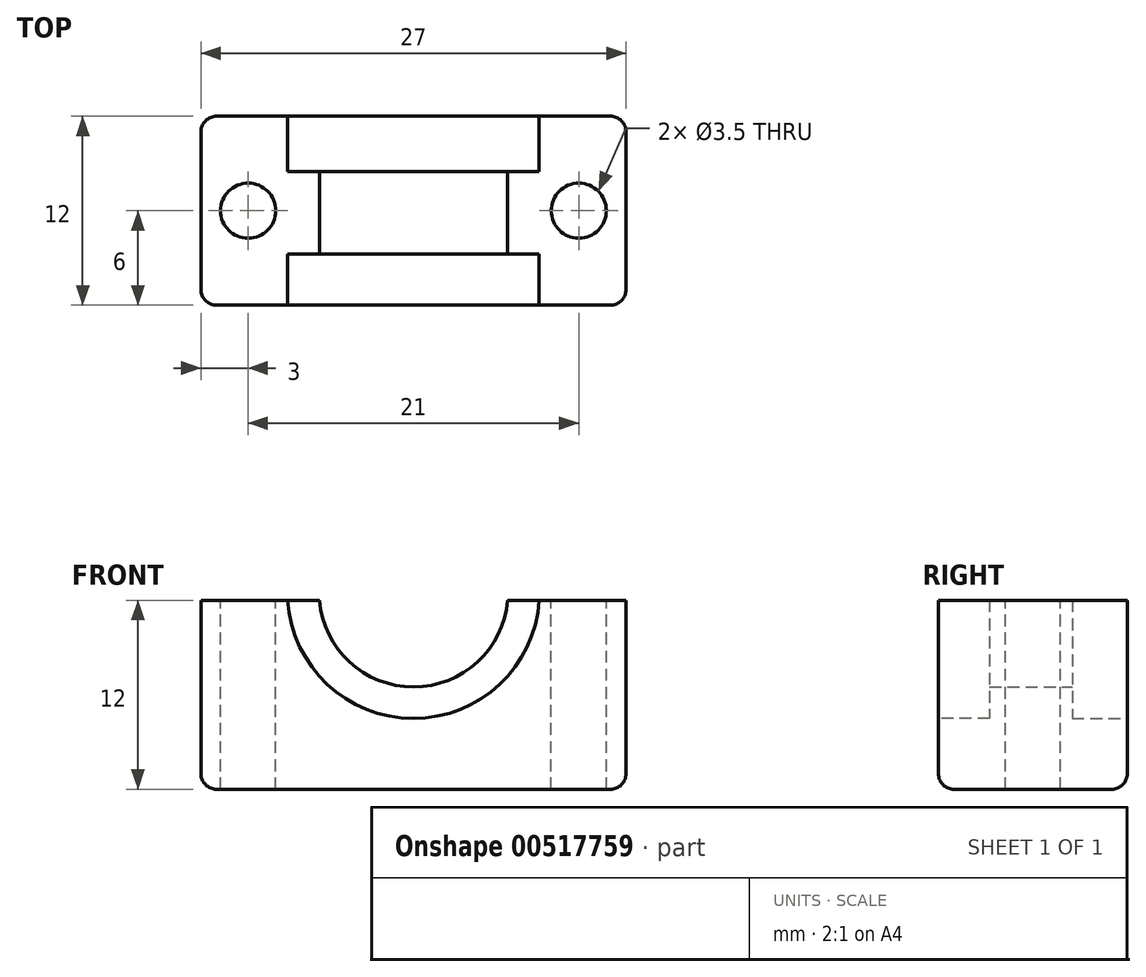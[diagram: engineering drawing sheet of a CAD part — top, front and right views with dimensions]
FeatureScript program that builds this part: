
annotation { "Feature Type Name" : "Feature", "Feature Type Description" : "" }
export const myFeature = defineFeature(function(context is Context, id is Id, definition is map)
    precondition{}
    {
        {
            var Q0;
            Q0=qCreatedBy(makeId("Top.planeOp"),FACE);
            var sketch = newSketch(context, id + "F0", { "sketchPlane" : qUnion([Q0])});
            skLineSegment(sketch, "E0.bottom", {"start": v(13.5, 6) * mm, "end": v(-13.5, 6) * mm});
            skLineSegment(sketch, "E0.top", {"start": v(13.5, -6) * mm, "end": v(-13.5, -6) * mm});
            skLineSegment(sketch, "E0.left", {"start": v(13.5, 6) * mm, "end": v(13.5, -6) * mm});
            skLineSegment(sketch, "E0.right", {"start": v(-13.5, 6) * mm, "end": v(-13.5, -6) * mm});
            skPoint(sketch, "E0.middle", {"position": v(0, 0) * mm});
            skSolve(sketch);
        }
        {
            var Q0;
            Q0 = qSketchRegion(id + "F0", true);
            extrude(context, id + "F1", {"entities" : qUnion([Q0]), "oppositeDirection" : true, "depth" : 12.5 * mm, "offsetDistance" : 25 * mm});
        }
        {
            var Q0;
            Q0=makeQuery(id+"F1.opExtrude","SWEPT_FACE",FACE,{"disambiguationData":[OSD([sQuery(id+"F0.wireOp",EDGE,"E0.top")])]});
            var sketch = newSketch(context, id + "F2", { "sketchPlane" : qUnion([Q0])});
            skArc(sketch, "E1", {"start": v(-8, 0) * mm, "mid": v(0, -8) * mm, "end": v(8, 0) * mm});
            skLineSegment(sketch, "E2", {"start": v(-28.38, 0) * mm, "end": v(31.21, 0) * mm, "construction": true});
            skLineSegment(sketch, "E3", {"start": v(-8, 0) * mm, "end": v(8, 0) * mm});
            skSolve(sketch);
        }
        {
            var Q0;
            Q0 = qSketchRegion(id + "F2", true);
            extrude(context, id + "F3", {"entities" : qUnion([Q0]), "operationType" : NewBodyOperationType.REMOVE, "oppositeDirection" : true, "depth" : 3.25 * mm, "offsetDistance" : 25 * mm});
        }
        {
            var Q0;
            Q0=makeQuery(id+"F1.opExtrude","SWEPT_FACE",FACE,{"disambiguationData":[OSD([sQuery(id+"F0.wireOp",EDGE,"E0.bottom")])]});
            var sketch = newSketch(context, id + "F4", { "sketchPlane" : qUnion([Q0])});
            skArc(sketch, "E4", {"start": v(-8, 0) * mm, "mid": v(0, -8) * mm, "end": v(8, 0) * mm});
            skLineSegment(sketch, "E5", {"start": v(-8, 0) * mm, "end": v(8, 0) * mm});
            skSolve(sketch);
        }
        {
            var Q0;
            Q0 = qSketchRegion(id + "F4", true);
            extrude(context, id + "F5", {"entities" : qUnion([Q0]), "operationType" : NewBodyOperationType.REMOVE, "oppositeDirection" : true, "depth" : 3.5 * mm, "offsetDistance" : 25 * mm});
        }
        {
            var Q0;
            Q0=makeQuery(id+"F5.boolean.opBoolean","COPY",FACE,{"derivedFrom":makeQuery(id+"F5.opExtrude","CAP_FACE",FACE,{"disambiguationData":[OSD([sQuery(id+"F4.wireOp",EDGE,"E4"),sQuery(id+"F4.wireOp",EDGE,"E5")])],"isStart":false})});
            var sketch = newSketch(context, id + "F6", { "sketchPlane" : qUnion([Q0])});
            skCircle(sketch, "E6", {"center": v(0, 0) * mm, "radius": 6 * mm});
            skSolve(sketch);
        }
        {
            var Q0;
            Q0 = qSketchRegion(id + "F6", true);
            extrude(context, id + "F7", {"entities" : qUnion([Q0]), "operationType" : NewBodyOperationType.REMOVE, "oppositeDirection" : true, "depth" : 25 * mm, "offsetDistance" : 25 * mm});
        }
        {
            var Q0;
            {var subQ1=sQuery(id+"F0.wireOp",EDGE,"E0.left");var subQ2=sQuery(id+"F0.wireOp",EDGE,"E0.top");var subQ3=sQuery(id+"F0.wireOp",EDGE,"E0.bottom");Q0=makeQuery(id+"F7.boolean.opBoolean","SPLIT",FACE,{"disambiguationData":[TD([makeQuery(id+"F1.opExtrude","SWEPT_FACE",FACE,{"disambiguationData":[OSD([subQ1])]})])],"derivedFrom":makeQuery(id+"F1.opExtrude","CAP_FACE",FACE,{"disambiguationData":[OSD([subQ3,subQ2,subQ1,sQuery(id+"F0.wireOp",EDGE,"E0.right")])],"isStart":true})});}
            var sketch = newSketch(context, id + "F8", { "sketchPlane" : qUnion([Q0])});
            skLineSegment(sketch, "E7", {"start": v(0, -16.55) * mm, "end": v(0, 25.84) * mm, "construction": true});
            skLineSegment(sketch, "E8", {"start": v(10.5, -14.89) * mm, "end": v(10.5, 18.46) * mm, "construction": true});
            skLineSegment(sketch, "E9", {"start": v(20.26, 0) * mm, "end": v(-33.56, 0) * mm, "construction": true});
            skLineSegment(sketch, "E10", {"start": v(-10.5, -18.93) * mm, "end": v(-10.5, 20.84) * mm, "construction": true});
            skCircle(sketch, "E11", {"center": v(10.5, 0) * mm, "radius": 1.75 * mm});
            skCircle(sketch, "E12", {"center": v(-10.5, 0) * mm, "radius": 1.75 * mm});
            skSolve(sketch);
        }
        {
            var Q0;
            Q0 = qSketchRegion(id + "F8", true);
            extrude(context, id + "F9", {"entities" : qUnion([Q0]), "operationType" : NewBodyOperationType.REMOVE, "oppositeDirection" : true, "depth" : 25 * mm, "offsetDistance" : 25 * mm});
        }
        {
            var Q0;
            Q0=makeQuery(id+"F1.opExtrude","SWEPT_FACE",FACE,{"disambiguationData":[OSD([sQuery(id+"F0.wireOp",EDGE,"E0.right")])]});
            var sketch = newSketch(context, id + "F10", { "sketchPlane" : qUnion([Q0])});
            skLineSegment(sketch, "E13", {"start": v(-6, -0.5) * mm, "end": v(6, -0.5) * mm});
            skLineSegment(sketch, "E14.0", {"start": v(-6, 0) * mm, "end": v(6, 0) * mm});
            skLineSegment(sketch, "E15.0", {"start": v(-6, -12.5) * mm, "end": v(-6, 0) * mm});
            skLineSegment(sketch, "E16.0", {"start": v(6, -12.5) * mm, "end": v(6, 0) * mm});
            skSolve(sketch);
        }
        {
            var Q0;
            {var subQ0=sQuery(id+"F10.wireOp",EDGE,"E13");Q0=makeQuery(id+"F10.imprint","IMPRINT",FACE,{"disambiguationData":[TD([[makeQuery(id+"F10.imprint","IMPRINT",EDGE,{"derivedFrom":subQ0}),1.0]])]});}
            extrude(context, id + "F11", {"entities" : qUnion([Q0]), "operationType" : NewBodyOperationType.REMOVE, "oppositeDirection" : true, "depth" : 31 * mm, "offsetDistance" : 25 * mm});
        }
        {
            var Q0;
            Q0=makeQuery(id+"F1.opExtrude","SWEPT_EDGE",EDGE,{"disambiguationData":[OSD([sQuery(id+"F0.wireOp",EDGE,"E0.top"),sQuery(id+"F0.wireOp",EDGE,"E0.right")])]});
            var Q1;
            Q1=makeQuery(id+"F1.opExtrude","SWEPT_EDGE",EDGE,{"disambiguationData":[OSD([sQuery(id+"F0.wireOp",EDGE,"E0.bottom"),sQuery(id+"F0.wireOp",EDGE,"E0.right")])]});
            var Q2;
            Q2=makeQuery(id+"F1.opExtrude","CAP_EDGE",EDGE,{"disambiguationData":[OSD([sQuery(id+"F0.wireOp",EDGE,"E0.right")])],"isStart":false});
            var Q3;
            Q3=makeQuery(id+"F1.opExtrude","CAP_EDGE",EDGE,{"disambiguationData":[OSD([sQuery(id+"F0.wireOp",EDGE,"E0.top")])],"isStart":false});
            var Q4;
            Q4=makeQuery(id+"F1.opExtrude","CAP_EDGE",EDGE,{"disambiguationData":[OSD([sQuery(id+"F0.wireOp",EDGE,"E0.bottom")])],"isStart":false});
            var Q5;
            Q5=makeQuery(id+"F1.opExtrude","SWEPT_EDGE",EDGE,{"disambiguationData":[OSD([sQuery(id+"F0.wireOp",EDGE,"E0.top"),sQuery(id+"F0.wireOp",EDGE,"E0.left")])]});
            var Q6;
            Q6=makeQuery(id+"F1.opExtrude","SWEPT_EDGE",EDGE,{"disambiguationData":[OSD([sQuery(id+"F0.wireOp",EDGE,"E0.bottom"),sQuery(id+"F0.wireOp",EDGE,"E0.left")])]});
            var Q7;
            Q7=makeQuery(id+"F1.opExtrude","CAP_EDGE",EDGE,{"disambiguationData":[OSD([sQuery(id+"F0.wireOp",EDGE,"E0.left")])],"isStart":false});
            fillet(context, id + "F12", {"entities" : qUnion([Q0, Q1, Q2, Q3, Q4, Q5, Q6, Q7]), "radius" : 1 * mm, "tangentPropagation" : true, "allowEdgeOverflow" : false});
        }
    });
